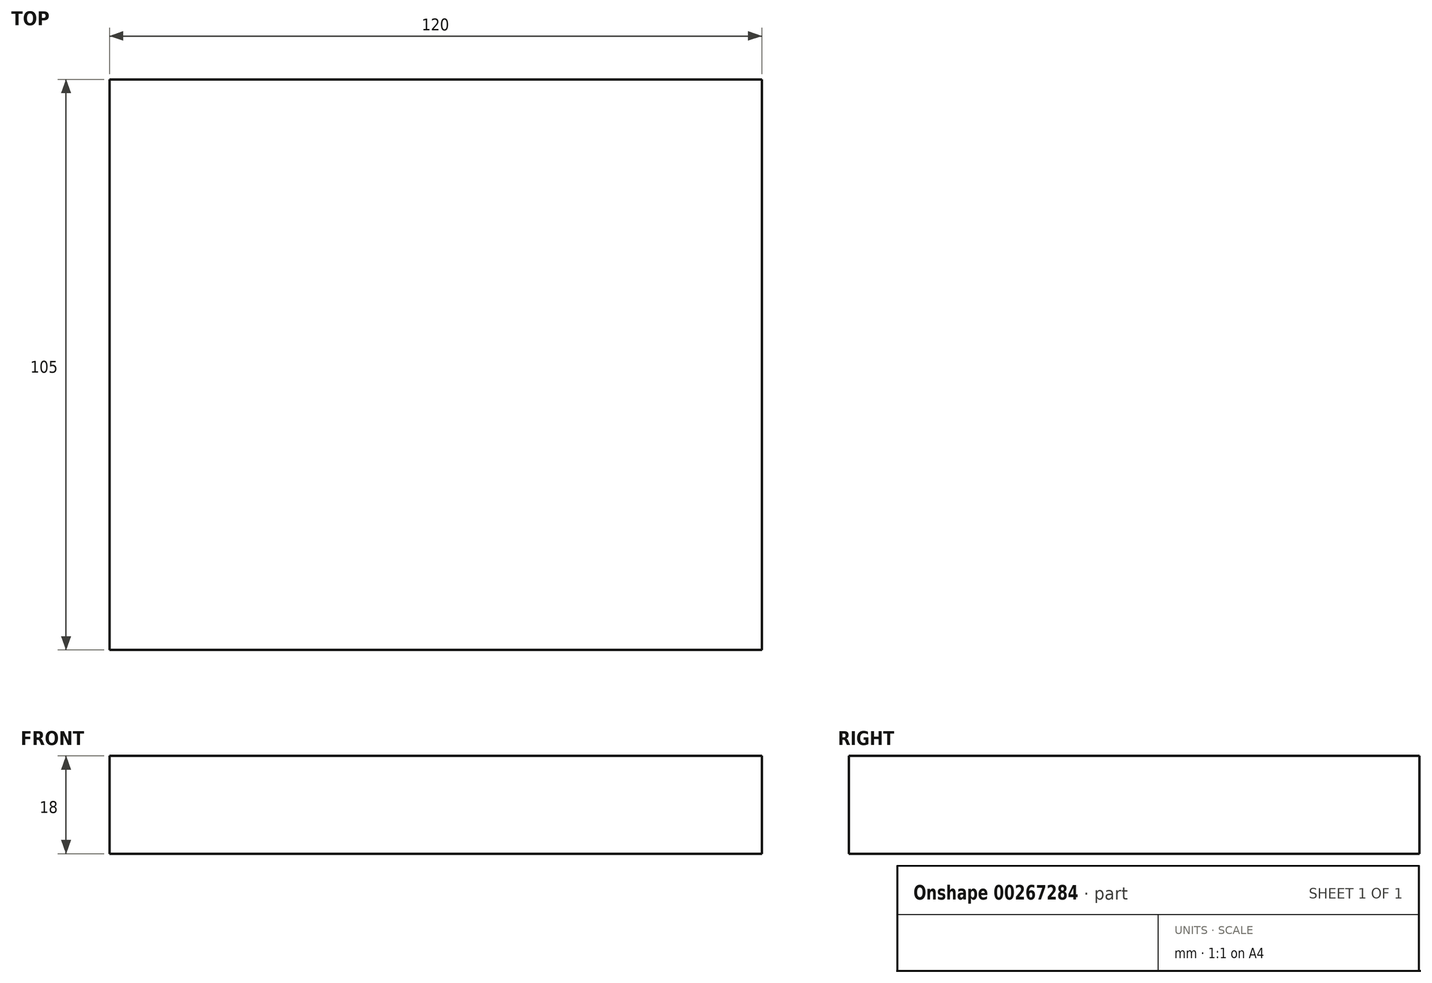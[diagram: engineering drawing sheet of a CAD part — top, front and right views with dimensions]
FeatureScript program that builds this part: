
annotation { "Feature Type Name" : "Feature", "Feature Type Description" : "" }
export const myFeature = defineFeature(function(context is Context, id is Id, definition is map)
    precondition{}
    {
        {
            var Q0;
            Q0=qCreatedBy(makeId("Top.planeOp"),FACE);
            var sketch = newSketch(context, id + "F0", { "sketchPlane" : qUnion([Q0])});
            skLineSegment(sketch, "E0.bottom", {"start": v(60, 52.5) * mm, "end": v(-60, 52.5) * mm});
            skLineSegment(sketch, "E0.top", {"start": v(60, -52.5) * mm, "end": v(-60, -52.5) * mm});
            skLineSegment(sketch, "E0.left", {"start": v(60, 52.5) * mm, "end": v(60, -52.5) * mm});
            skLineSegment(sketch, "E0.right", {"start": v(-60, 52.5) * mm, "end": v(-60, -52.5) * mm});
            skPoint(sketch, "E0.middle", {"position": v(0, 0) * mm});
            skSolve(sketch);
        }
        {
            var Q0;
            Q0=makeQuery(id+"F0.imprint","IMPRINT",FACE,{"disambiguationData":[TD([[makeQuery(id+"F0.imprint","IMPRINT",EDGE,{"derivedFrom":sQuery(id+"F0.wireOp",EDGE,"E0.bottom")}),1.0]])]});
            extrude(context, id + "F1", {"entities" : qUnion([Q0]), "depth" : 18 * mm});
        }
    });
